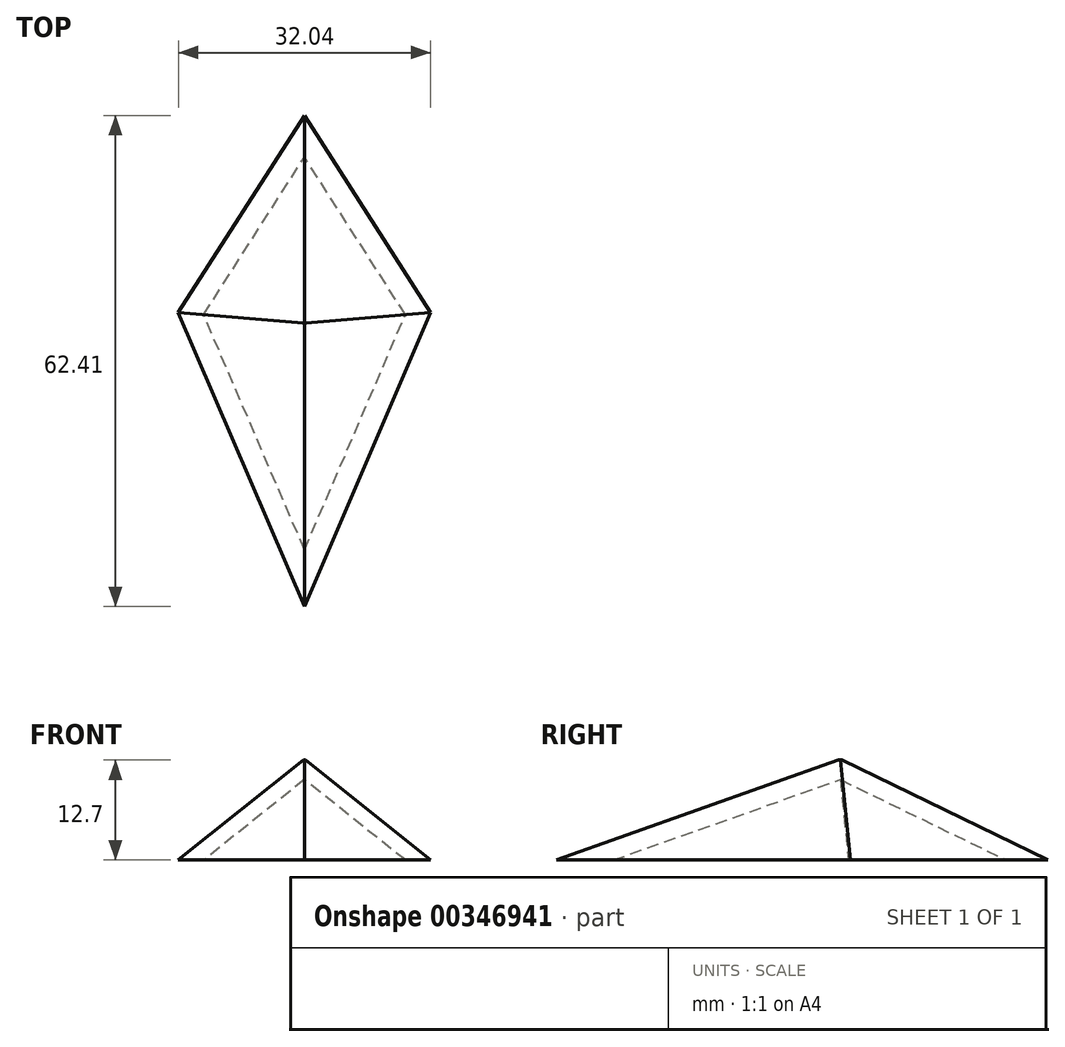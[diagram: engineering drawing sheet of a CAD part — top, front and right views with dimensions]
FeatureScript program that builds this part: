
annotation { "Feature Type Name" : "Feature", "Feature Type Description" : "" }
export const myFeature = defineFeature(function(context is Context, id is Id, definition is map)
    precondition{}
    {
        {
            var Q0;
            Q0=qCreatedBy(makeId("Top.planeOp"),FACE);
            var sketch = newSketch(context, id + "F0", { "sketchPlane" : qUnion([Q0])});
            skLineSegment(sketch, "E0", {"start": v(0, 25.5) * mm, "end": v(-16.3, 0) * mm});
            skLineSegment(sketch, "E1", {"start": v(-16.3, 0) * mm, "end": v(0, -38) * mm});
            skLineSegment(sketch, "E2.MirrorCS", {"start": v(0, 25.5) * mm, "end": v(16.3, 0) * mm});
            skLineSegment(sketch, "E3.MirrorCS", {"start": v(16.3, 0) * mm, "end": v(0, -38) * mm});
            skSolve(sketch);
        }
        {
            var Q0;
            Q0=makeQuery(id+"F0.imprint","IMPRINT",FACE,{"disambiguationData":[TD([[makeQuery(id+"F0.imprint","IMPRINT",EDGE,{"derivedFrom":sQuery(id+"F0.wireOp",EDGE,"E0")}),1.0]])]});
            extrude(context, id + "F1", {"entities" : qUnion([Q0]), "depth" : 12.7 * mm});
        }
        {
            var Q0;
            Q0=makeQuery(id+"F1.opExtrude","CAP_FACE",FACE,{"disambiguationData":[OSD([sQuery(id+"F0.wireOp",EDGE,"E0"),sQuery(id+"F0.wireOp",EDGE,"E1"),sQuery(id+"F0.wireOp",EDGE,"E2.MirrorCS"),sQuery(id+"F0.wireOp",EDGE,"E3.MirrorCS")])],"isStart":false});
            chamfer(context, id + "F2", {"entities" : qUnion([Q0]), "chamferType" : ChamferType.OFFSET_ANGLE, "width" : 14.35 * mm, "oppositeDirection" : false, "angle" : 42 * degree, "tangentPropagation" : true});
        }
        {
            var Q0;
            Q0=makeQuery(id+"F1.opExtrude","CAP_FACE",FACE,{"disambiguationData":[OSD([sQuery(id+"F0.wireOp",EDGE,"E0"),sQuery(id+"F0.wireOp",EDGE,"E1"),sQuery(id+"F0.wireOp",EDGE,"E2.MirrorCS"),sQuery(id+"F0.wireOp",EDGE,"E3.MirrorCS")])],"isStart":true});
            shell(context, id + "F3", {"entities" : qUnion([Q0]), "thickness" : 1.9 * mm});
        }
    });
